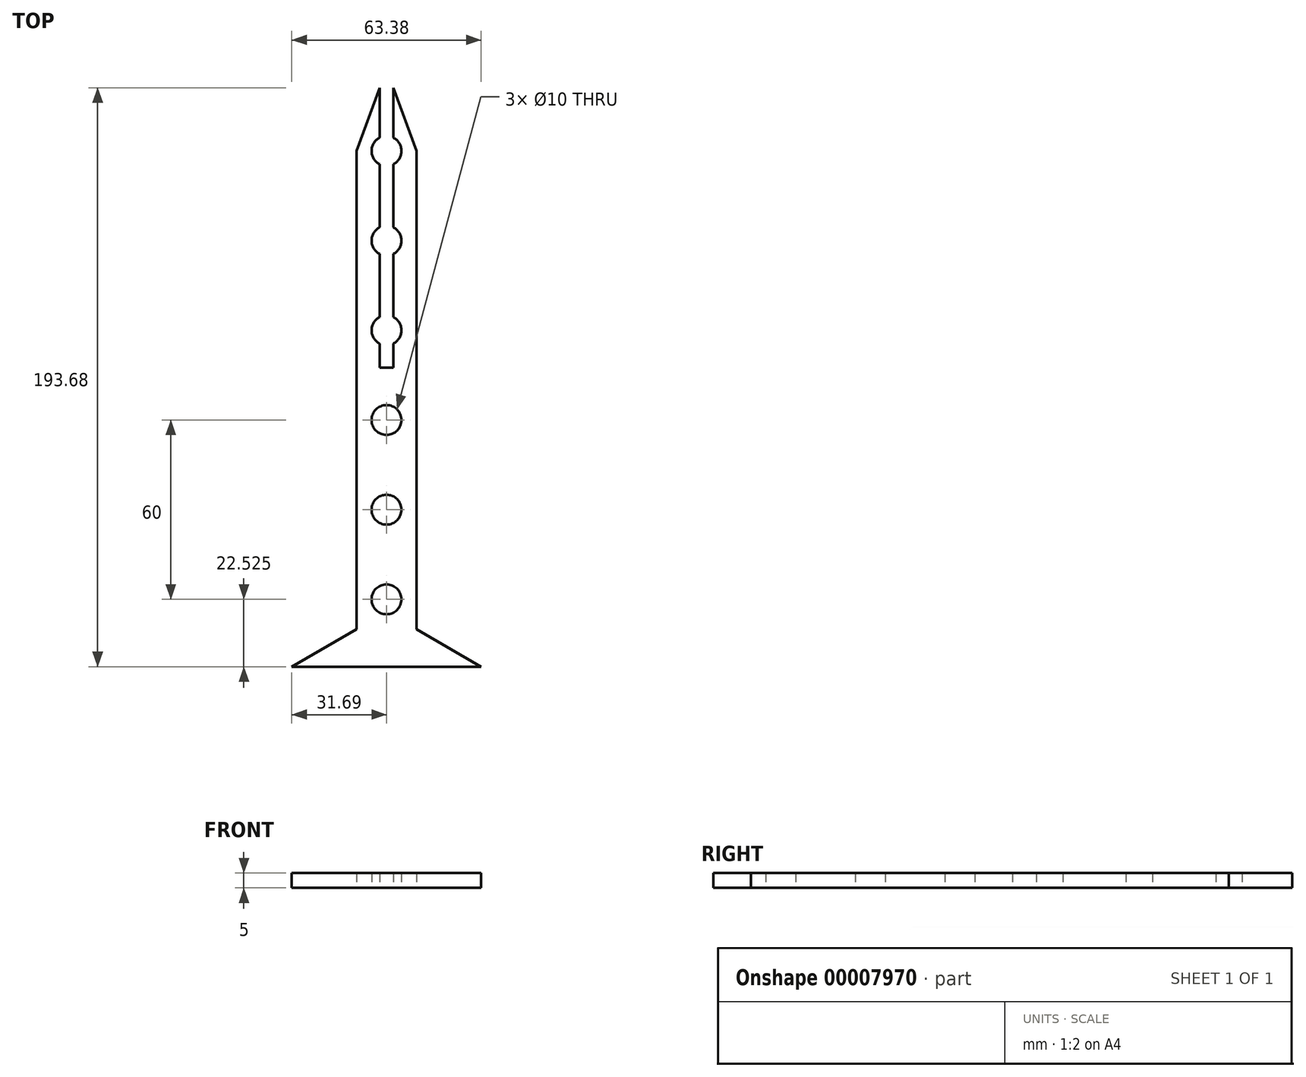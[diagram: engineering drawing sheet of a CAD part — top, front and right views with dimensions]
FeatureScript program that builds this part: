
annotation { "Feature Type Name" : "Feature", "Feature Type Description" : "" }
export const myFeature = defineFeature(function(context is Context, id is Id, definition is map)
    precondition{}
    {
        {
            var Q0;
            Q0=qCreatedBy(makeId("Top.planeOp"),FACE);
            var sketch = newSketch(context, id + "F0", { "sketchPlane" : qUnion([Q0])});
            skLineSegment(sketch, "E0.left", {"start": v(-10, -27.47) * mm, "end": v(-10, -187.47) * mm});
            skLineSegment(sketch, "E1", {"start": v(-10, -27.47) * mm, "end": v(-2.3, -6.32) * mm});
            skLineSegment(sketch, "E2", {"start": v(-10, -187.47) * mm, "end": v(-31.7, -200) * mm});
            skLineSegment(sketch, "E3", {"start": v(-31.7, -200) * mm, "end": v(-2.3, -200) * mm});
            skLineSegment(sketch, "E4.0.MirrorCS", {"start": v(10, -27.47) * mm, "end": v(2.3, -6.32) * mm});
            skLineSegment(sketch, "E5.0.MirrorCS", {"start": v(10, -27.47) * mm, "end": v(10, -187.47) * mm});
            skLineSegment(sketch, "E6.0.MirrorCS", {"start": v(10, -187.47) * mm, "end": v(31.7, -200) * mm});
            skLineSegment(sketch, "E7.0.MirrorCS", {"start": v(31.7, -200) * mm, "end": v(2.3, -200) * mm});
            skArc(sketch, "E8", {"start": v(2.3, -31.91) * mm, "mid": v(5, -27.47) * mm, "end": v(2.3, -23.04) * mm});
            skArc(sketch, "E9.0.1.0", {"start": v(2.3, -61.91) * mm, "mid": v(5, -57.47) * mm, "end": v(2.3, -53.04) * mm});
            skArc(sketch, "E9.0.2.0", {"start": v(2.3, -91.91) * mm, "mid": v(5, -87.47) * mm, "end": v(2.3, -83.04) * mm});
            skCircle(sketch, "E9.0.3.0", {"center": v(0, -117.47) * mm, "radius": 5 * mm});
            skCircle(sketch, "E9.0.4.0", {"center": v(0, -147.47) * mm, "radius": 5 * mm});
            skCircle(sketch, "E9.0.5.0", {"center": v(0, -177.47) * mm, "radius": 5 * mm});
            skLineSegment(sketch, "E9.direction1", {"start": v(0, -27.47) * mm, "end": v(25, -27.47) * mm, "construction": true});
            skLineSegment(sketch, "E9.direction2", {"start": v(0, -27.47) * mm, "end": v(0, -57.47) * mm, "construction": true});
            skLineSegment(sketch, "E10", {"start": v(-2.3, -200) * mm, "end": v(2.3, -200) * mm});
            skLineSegment(sketch, "E11.bottom", {"start": v(-2.3, -99.97) * mm, "end": v(2.3, -99.97) * mm});
            skLineSegment(sketch, "E11.left", {"start": v(-2.3, -99.97) * mm, "end": v(-2.3, -91.91) * mm});
            skLineSegment(sketch, "E11.right", {"start": v(2.3, -99.97) * mm, "end": v(2.3, -91.91) * mm});
            skLineSegment(sketch, "E12.trimOffspring", {"start": v(2.3, -83.04) * mm, "end": v(2.3, -61.91) * mm});
            skArc(sketch, "E13.trimOffspring", {"start": v(-2.3, -83.04) * mm, "mid": v(-5, -87.47) * mm, "end": v(-2.3, -91.91) * mm});
            skLineSegment(sketch, "E14.trimOffspring", {"start": v(-2.3, -83.04) * mm, "end": v(-2.3, -61.91) * mm});
            skLineSegment(sketch, "E15.trimOffspring", {"start": v(-2.3, -53.04) * mm, "end": v(-2.3, -31.91) * mm});
            skLineSegment(sketch, "E16.trimOffspring", {"start": v(2.3, -53.04) * mm, "end": v(2.3, -31.91) * mm});
            skArc(sketch, "E17.trimOffspring", {"start": v(-2.3, -53.04) * mm, "mid": v(-5, -57.47) * mm, "end": v(-2.3, -61.91) * mm});
            skLineSegment(sketch, "E18.trimOffspring", {"start": v(-2.3, -23.04) * mm, "end": v(-2.3, -6.32) * mm});
            skLineSegment(sketch, "E19.trimOffspring", {"start": v(2.3, -23.04) * mm, "end": v(2.3, -6.32) * mm});
            skArc(sketch, "E20.trimOffspring", {"start": v(-2.3, -23.04) * mm, "mid": v(-5, -27.47) * mm, "end": v(-2.3, -31.91) * mm});
            skPoint(sketch, "E21.orphan", {"position": v(2.3, 0) * mm});
            skPoint(sketch, "E22.orphan", {"position": v(0, 0) * mm});
            skLineSegment(sketch, "E23", {"start": v(0, 0) * mm, "end": v(-2.3, -6.32) * mm, "construction": true});
            skLineSegment(sketch, "E24", {"start": v(0, 0) * mm, "end": v(2.3, -6.32) * mm, "construction": true});
            skSolve(sketch);
        }
        {
            var Q0;
            Q0=qSketchRegion(id+"F0",true);
            extrude(context, id + "F1", {"entities" : qUnion([Q0]), "depth" : 5 * mm});
        }
    });
